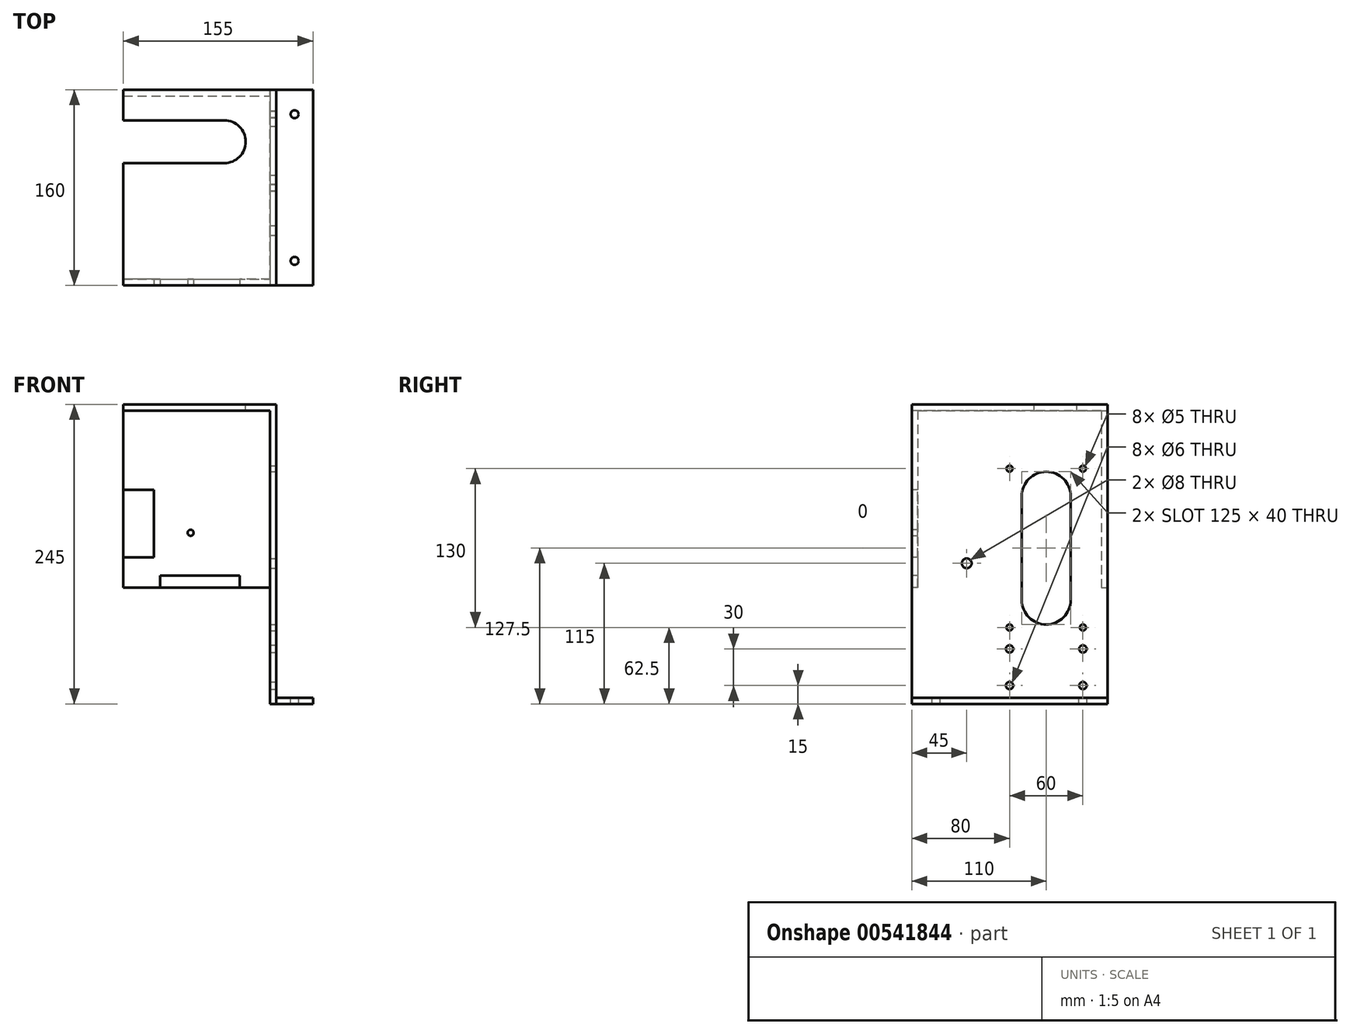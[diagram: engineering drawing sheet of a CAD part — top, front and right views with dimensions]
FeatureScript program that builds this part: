
annotation { "Feature Type Name" : "Feature", "Feature Type Description" : "" }
export const myFeature = defineFeature(function(context is Context, id is Id, definition is map)
    precondition{}
    {
        {
            var Q0;
            Q0=qCreatedBy(makeId("Front.planeOp"),FACE);
            var sketch = newSketch(context, id + "F0", { "sketchPlane" : qUnion([Q0])});
            skLineSegment(sketch, "E0.bottom", {"start": v(-62.5, 122.5) * mm, "end": v(62.5, 122.5) * mm});
            skLineSegment(sketch, "E0.right", {"start": v(62.5, 122.5) * mm, "end": v(62.5, -122.5) * mm});
            skPoint(sketch, "E0.middle", {"position": v(0, 0) * mm});
            skLineSegment(sketch, "E1.0", {"start": v(-62.5, 117.5) * mm, "end": v(57.5, 117.5) * mm});
            skLineSegment(sketch, "E2.0", {"start": v(57.5, 117.5) * mm, "end": v(57.5, -122.5) * mm});
            skLineSegment(sketch, "E3.trimOffspring", {"start": v(62.5, 117.5) * mm, "end": v(62.5, 117.5) * mm});
            skLineSegment(sketch, "E4", {"start": v(-62.5, 122.5) * mm, "end": v(-62.5, 117.5) * mm});
            skLineSegment(sketch, "E5", {"start": v(62.5, -122.5) * mm, "end": v(57.5, -122.5) * mm});
            skSolve(sketch);
        }
        {
            var Q0;
            Q0=makeQuery(id+"F0.imprint","IMPRINT",FACE,{"disambiguationData":[TD([[makeQuery(id+"F0.imprint","IMPRINT",EDGE,{"derivedFrom":sQuery(id+"F0.wireOp",EDGE,"E1.0")}),1.0]])]});
            var Q1;
            {var subQ3=sQuery(id+"F0.wireOp",EDGE,"E3.trimOffspring");Q1=makeQuery(id+"F0.imprint","IMPRINT",FACE,{"disambiguationData":[TD([[makeQuery(id+"F0.imprint","IMPRINT",EDGE,{"derivedFrom":subQ3}),-1.0]])]});}
            var Q2;
            {var subQ5=sQuery(id+"F0.wireOp",EDGE,"E3.trimOffspring");Q2=makeQuery(id+"F0.imprint","IMPRINT",FACE,{"disambiguationData":[TD([[makeQuery(id+"F0.imprint","IMPRINT",EDGE,{"derivedFrom":subQ5}),1.0]])]});}
            extrude(context, id + "F1", {"entities" : qUnion([Q0, Q1, Q2]), "depth" : 160 * mm, "offsetDistance" : 25 * mm});
        }
        {
            var Q0;
            Q0=makeQuery(id+"F1.opExtrude","CAP_FACE",FACE,{"disambiguationData":[OSD([sQuery(id+"F0.wireOp",EDGE,"E0.bottom"),sQuery(id+"F0.wireOp",EDGE,"E0.right"),sQuery(id+"F0.wireOp",EDGE,"E1.0"),sQuery(id+"F0.wireOp",EDGE,"E2.0"),sQuery(id+"F0.wireOp",EDGE,"E4"),sQuery(id+"F0.wireOp",EDGE,"E5")])],"isStart":false});
            var sketch = newSketch(context, id + "F2", { "sketchPlane" : qUnion([Q0])});
            skLineSegment(sketch, "E6.top", {"start": v(62.5, -27.5) * mm, "end": v(-62.5, -27.5) * mm});
            skLineSegment(sketch, "E6.left", {"start": v(62.5, 122.5) * mm, "end": v(62.5, -27.5) * mm});
            skLineSegment(sketch, "E6.right", {"start": v(-62.5, 122.5) * mm, "end": v(-62.5, -27.5) * mm});
            skLineSegment(sketch, "E7", {"start": v(62.5, 122.5) * mm, "end": v(-62.5, 122.5) * mm});
            skSolve(sketch);
        }
        {
            var Q0;
            Q0 = qSketchRegion(id + "F2", true);
            extrude(context, id + "F3", {"entities" : qUnion([Q0]), "operationType" : NewBodyOperationType.ADD, "oppositeDirection" : true, "depth" : 5 * mm, "offsetDistance" : 25 * mm});
        }
        {
            var Q0;
            Q0=makeQuery(id+"F3.boolean.opBoolean","MERGE",FACE,{"derivedFrom":[makeQuery(id+"F1.opExtrude","CAP_FACE",FACE,{"disambiguationData":[OSD([sQuery(id+"F0.wireOp",EDGE,"E0.bottom"),sQuery(id+"F0.wireOp",EDGE,"E0.right"),sQuery(id+"F0.wireOp",EDGE,"E1.0"),sQuery(id+"F0.wireOp",EDGE,"E2.0"),sQuery(id+"F0.wireOp",EDGE,"E4"),sQuery(id+"F0.wireOp",EDGE,"E5")])],"isStart":false}),makeQuery(id+"F3.opExtrude","CAP_FACE",FACE,{"disambiguationData":[OSD([sQuery(id+"F2.wireOp",EDGE,"E6.top"),sQuery(id+"F2.wireOp",EDGE,"E6.left"),sQuery(id+"F2.wireOp",EDGE,"E6.right"),sQuery(id+"F2.wireOp",EDGE,"E7")])],"isStart":true})]});
            cPlane(context, id + "F4", {"entities" : qUnion([Q0]), "cplaneType" : CPlaneType.OFFSET, "offset" : 80 * mm, "oppositeDirection" : true, "width" : 150 * mm, "height" : 150 * mm});
        }
        {
            var Q0;
            Q0=makeQuery(id+"F1.opExtrude","SWEPT_BODY",BODY,{"disambiguationData":[OSD([sQuery(id+"F0.wireOp",EDGE,"E0.bottom"),sQuery(id+"F0.wireOp",EDGE,"E0.right"),sQuery(id+"F0.wireOp",EDGE,"E1.0"),sQuery(id+"F0.wireOp",EDGE,"E2.0"),sQuery(id+"F0.wireOp",EDGE,"E4"),sQuery(id+"F0.wireOp",EDGE,"E5")])]});
            var Q1;
            Q1=qCreatedBy(id+"F4.planeOp",FACE);
            mirror(context, id + "F5", {"entities" : qUnion([Q0]), "mirrorPlane" : qUnion([Q1])});
        }
        {
            var Q0;
            Q0=makeQuery(id+"F1.opExtrude","SWEPT_FACE",FACE,{"disambiguationData":[OSD([sQuery(id+"F0.wireOp",EDGE,"E0.bottom")])]});
            var sketch = newSketch(context, id + "F6", { "sketchPlane" : qUnion([Q0])});
            skLineSegment(sketch, "E8.0", {"start": v(-62.5, -60) * mm, "end": v(20, -60) * mm});
            skLineSegment(sketch, "E9.0", {"start": v(-62.5, -25) * mm, "end": v(20, -25) * mm});
            skLineSegment(sketch, "E10", {"start": v(-62.5, -25) * mm, "end": v(-62.5, -60) * mm});
            skArc(sketch, "E11", {"start": v(20, -60) * mm, "mid": v(37.5, -42.5) * mm, "end": v(20, -25) * mm});
            skSolve(sketch);
        }
        {
            var Q0;
            Q0 = qSketchRegion(id + "F6", true);
            extrude(context, id + "F7", {"entities" : qUnion([Q0]), "operationType" : NewBodyOperationType.REMOVE, "oppositeDirection" : true, "depth" : 25 * mm, "offsetDistance" : 25 * mm});
        }
        {
            var Q0;
            Q0=makeQuery(id+"F1.opExtrude","SWEPT_FACE",FACE,{"disambiguationData":[OSD([sQuery(id+"F0.wireOp",EDGE,"E0.right")])]});
            var sketch = newSketch(context, id + "F8", { "sketchPlane" : qUnion([Q0])});
            skLineSegment(sketch, "E12.bottom", {"start": v(-160, -122.5) * mm, "end": v(0, -122.5) * mm});
            skLineSegment(sketch, "E12.top", {"start": v(-160, -117.5) * mm, "end": v(0, -117.5) * mm});
            skLineSegment(sketch, "E12.left", {"start": v(-160, -122.5) * mm, "end": v(-160, -117.5) * mm});
            skLineSegment(sketch, "E12.right", {"start": v(0, -122.5) * mm, "end": v(0, -117.5) * mm});
            skSolve(sketch);
        }
        {
            var Q0;
            Q0=makeQuery(id+"F8.imprint","IMPRINT",FACE,{"disambiguationData":[TD([[makeQuery(id+"F8.imprint","IMPRINT",EDGE,{"derivedFrom":sQuery(id+"F8.wireOp",EDGE,"E12.bottom")}),1.0]])]});
            extrude(context, id + "F9", {"entities" : qUnion([Q0]), "depth" : 30 * mm, "offsetDistance" : 25 * mm});
        }
        {
            var Q0;
            Q0=makeQuery(id+"F9.opExtrude","SWEPT_FACE",FACE,{"disambiguationData":[OSD([sQuery(id+"F8.wireOp",EDGE,"E12.top")])]});
            var sketch = newSketch(context, id + "F10", { "sketchPlane" : qUnion([Q0])});
            skCircle(sketch, "E13", {"center": v(77.5, -140) * mm, "radius": 3.25 * mm});
            skCircle(sketch, "E14", {"center": v(77.5, -20) * mm, "radius": 3.25 * mm});
            skSolve(sketch);
        }
        {
            var Q0;
            Q0 = qSketchRegion(id + "F10", true);
            extrude(context, id + "F11", {"entities" : qUnion([Q0]), "operationType" : NewBodyOperationType.REMOVE, "oppositeDirection" : true, "depth" : 25 * mm, "offsetDistance" : 25 * mm});
        }
        {
            var Q0;
            Q0=makeQuery(id+"F1.opExtrude","SWEPT_FACE",FACE,{"disambiguationData":[OSD([sQuery(id+"F0.wireOp",EDGE,"E0.right")])]});
            var sketch = newSketch(context, id + "F12", { "sketchPlane" : qUnion([Q0])});
            skLineSegment(sketch, "E15.0", {"start": v(-30, 47.5) * mm, "end": v(-30, -37.5) * mm});
            skLineSegment(sketch, "E16.0", {"start": v(-70, 47.5) * mm, "end": v(-70, -37.5) * mm});
            skArc(sketch, "E17", {"start": v(-30, 47.5) * mm, "mid": v(-50, 67.5) * mm, "end": v(-70, 47.5) * mm});
            skArc(sketch, "E18", {"start": v(-70, -37.5) * mm, "mid": v(-50, -57.5) * mm, "end": v(-30, -37.5) * mm});
            skSolve(sketch);
        }
        {
            var Q0;
            Q0=makeQuery(id+"F12.imprint","IMPRINT",FACE,{"disambiguationData":[TD([[makeQuery(id+"F12.imprint","IMPRINT",EDGE,{"derivedFrom":sQuery(id+"F12.wireOp",EDGE,"E15.0")}),-1.0]])]});
            extrude(context, id + "F13", {"entities" : qUnion([Q0]), "operationType" : NewBodyOperationType.REMOVE, "endBound" : BoundingType.UP_TO_NEXT, "oppositeDirection" : true, "depth" : 25 * mm, "offsetDistance" : 25 * mm});
        }
        {
            var Q0;
            Q0=makeQuery(id+"F1.opExtrude","SWEPT_FACE",FACE,{"disambiguationData":[OSD([sQuery(id+"F0.wireOp",EDGE,"E0.right")])]});
            var sketch = newSketch(context, id + "F14", { "sketchPlane" : qUnion([Q0])});
            skCircle(sketch, "E19", {"center": v(-80, 70) * mm, "radius": 2.5 * mm});
            skCircle(sketch, "E20", {"center": v(-20, 70) * mm, "radius": 2.5 * mm});
            skCircle(sketch, "E21.MirrorC", {"center": v(-20, -60) * mm, "radius": 2.5 * mm});
            skCircle(sketch, "E22.MirrorC", {"center": v(-80, -60) * mm, "radius": 2.5 * mm});
            skPoint(sketch, "E23.orphan", {"position": v(-50, -57.5) * mm});
            skPoint(sketch, "E24.trimOffspring.end.orphan", {"position": v(-160, 5) * mm});
            skSolve(sketch);
        }
        {
            var Q0;
            Q0 = qSketchRegion(id + "F14", true);
            extrude(context, id + "F15", {"entities" : qUnion([Q0]), "operationType" : NewBodyOperationType.REMOVE, "endBound" : BoundingType.UP_TO_NEXT, "oppositeDirection" : true, "depth" : 25 * mm, "offsetDistance" : 25 * mm});
        }
        {
            var Q0;
            Q0=makeQuery(id+"F3.boolean.opBoolean","MERGE",FACE,{"derivedFrom":[makeQuery(id+"F1.opExtrude","CAP_FACE",FACE,{"disambiguationData":[OSD([sQuery(id+"F0.wireOp",EDGE,"E0.bottom"),sQuery(id+"F0.wireOp",EDGE,"E0.right"),sQuery(id+"F0.wireOp",EDGE,"E1.0"),sQuery(id+"F0.wireOp",EDGE,"E2.0"),sQuery(id+"F0.wireOp",EDGE,"E4"),sQuery(id+"F0.wireOp",EDGE,"E5")])],"isStart":false}),makeQuery(id+"F3.opExtrude","CAP_FACE",FACE,{"disambiguationData":[OSD([sQuery(id+"F2.wireOp",EDGE,"E6.top"),sQuery(id+"F2.wireOp",EDGE,"E6.left"),sQuery(id+"F2.wireOp",EDGE,"E6.right"),sQuery(id+"F2.wireOp",EDGE,"E7")])],"isStart":true})]});
            var sketch = newSketch(context, id + "F16", { "sketchPlane" : qUnion([Q0])});
            skLineSegment(sketch, "E25.0", {"start": v(-62.5, 52.5) * mm, "end": v(-37.5, 52.5) * mm});
            skLineSegment(sketch, "E26.0", {"start": v(-62.5, -2.5) * mm, "end": v(-37.5, -2.5) * mm});
            skLineSegment(sketch, "E27.0", {"start": v(-37.5, 52.5) * mm, "end": v(-37.5, -2.5) * mm});
            skLineSegment(sketch, "E28", {"start": v(-62.5, 52.5) * mm, "end": v(-62.5, -2.5) * mm});
            skSolve(sketch);
        }
        {
            var Q0;
            Q0 = qSketchRegion(id + "F16", true);
            extrude(context, id + "F17", {"entities" : qUnion([Q0]), "operationType" : NewBodyOperationType.REMOVE, "endBound" : BoundingType.UP_TO_NEXT, "oppositeDirection" : true, "depth" : 25 * mm, "offsetDistance" : 25 * mm});
        }
        {
            var Q0;
            Q0=makeQuery(id+"F3.boolean.opBoolean","MERGE",FACE,{"derivedFrom":[makeQuery(id+"F1.opExtrude","CAP_FACE",FACE,{"disambiguationData":[OSD([sQuery(id+"F0.wireOp",EDGE,"E0.bottom"),sQuery(id+"F0.wireOp",EDGE,"E0.right"),sQuery(id+"F0.wireOp",EDGE,"E1.0"),sQuery(id+"F0.wireOp",EDGE,"E2.0"),sQuery(id+"F0.wireOp",EDGE,"E4"),sQuery(id+"F0.wireOp",EDGE,"E5")])],"isStart":false}),makeQuery(id+"F3.opExtrude","CAP_FACE",FACE,{"disambiguationData":[OSD([sQuery(id+"F2.wireOp",EDGE,"E6.top"),sQuery(id+"F2.wireOp",EDGE,"E6.left"),sQuery(id+"F2.wireOp",EDGE,"E6.right"),sQuery(id+"F2.wireOp",EDGE,"E7")])],"isStart":true})]});
            var sketch = newSketch(context, id + "F18", { "sketchPlane" : qUnion([Q0])});
            skCircle(sketch, "E29", {"center": v(-7.5, 17.5) * mm, "radius": 2.5 * mm});
            skPoint(sketch, "E30.orphan", {"position": v(-7.5, 117.5) * mm});
            skLineSegment(sketch, "E31.0", {"start": v(-32.5, -17.5) * mm, "end": v(-32.5, -27.5) * mm});
            skLineSegment(sketch, "E32.0", {"start": v(32.5, -17.5) * mm, "end": v(-32.5, -17.5) * mm});
            skLineSegment(sketch, "E33", {"start": v(32.5, -17.5) * mm, "end": v(32.5, -27.5) * mm});
            skLineSegment(sketch, "E34", {"start": v(32.5, -27.5) * mm, "end": v(-32.5, -27.5) * mm});
            skSolve(sketch);
        }
        {
            var Q0;
            Q0 = qSketchRegion(id + "F18", true);
            extrude(context, id + "F19", {"entities" : qUnion([Q0]), "operationType" : NewBodyOperationType.REMOVE, "endBound" : BoundingType.UP_TO_NEXT, "oppositeDirection" : true, "depth" : 25 * mm, "offsetDistance" : 25 * mm});
        }
        {
            var Q0;
            Q0=makeQuery(id+"F1.opExtrude","SWEPT_FACE",FACE,{"disambiguationData":[OSD([sQuery(id+"F0.wireOp",EDGE,"E0.right")])]});
            var sketch = newSketch(context, id + "F20", { "sketchPlane" : qUnion([Q0])});
            skCircle(sketch, "E35", {"center": v(-115, -7.5) * mm, "radius": 4 * mm});
            skCircle(sketch, "E36", {"center": v(-80, -77.5) * mm, "radius": 3 * mm});
            skCircle(sketch, "E37", {"center": v(-20, -77.5) * mm, "radius": 3 * mm});
            skCircle(sketch, "E38", {"center": v(-80, -107.5) * mm, "radius": 3 * mm});
            skCircle(sketch, "E39", {"center": v(-20, -107.5) * mm, "radius": 3 * mm});
            skSolve(sketch);
        }
        {
            var Q0;
            Q0 = qSketchRegion(id + "F20", true);
            extrude(context, id + "F21", {"entities" : qUnion([Q0]), "operationType" : NewBodyOperationType.REMOVE, "endBound" : BoundingType.UP_TO_NEXT, "oppositeDirection" : true, "depth" : 25 * mm, "offsetDistance" : 25 * mm});
        }
    });
